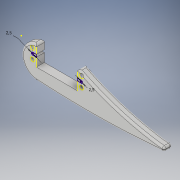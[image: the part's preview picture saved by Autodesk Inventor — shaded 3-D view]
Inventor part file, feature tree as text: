
AUTODESK INVENTOR PART (.ipt)
format: ipt  version: 2019 (Build 230136000, 136)  size: 200,192 bytes
history: native  units: mm
features: extrude x3, fillet x2, sketch x2, other x1
ambient origin geometry x8: Origin, YZ Plane, XZ Plane, XY Plane, X Axis, Y Axis, Z Axis, Center Point
bodies: Body1 (feature_tree)
feature tree (8):
  other  "Твердое тело1"
  extrude  "Выдавливание1"  Depth=143.0mm
  fillet  "Сопряжение1"  Radius=32.0mm
  fillet  "Сопряжение2"  Radius=15.0mm
  sketch  "Эскиз2"
  extrude  "Выдавливание2"  Depth=41.0mm
  extrude  "Выдавливание3"  Depth=6.0mm
  sketch  "Эскиз1"
